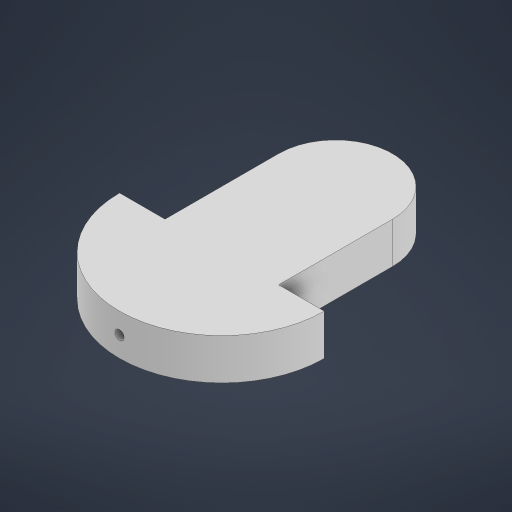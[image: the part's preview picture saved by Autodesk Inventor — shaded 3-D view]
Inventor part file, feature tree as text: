
AUTODESK INVENTOR PART (.ipt)
format: ipt  version: 2024 (Build 280153000, 153)  size: 178,176 bytes
history: native  units: mm
features: extrude x2, sketch x2, other x1, plane x1
ambient origin geometry x8: Origin, YZ Plane, XZ Plane, XY Plane, X Axis, Y Axis, Z Axis, Center Point
bodies: Body1 (feature_tree)
feature tree (6):
  other  "Sólido1"
  extrude  "Extrusión1"  Depth=90.0mm
  plane  "Plano de trabajo2"
  extrude  "Extrusión2"  Depth=4.0mm
  sketch  "Boceto1"  dims[d3=50.0mm d4=90.0mm]
  sketch  "Boceto2"  dims[d7=18.0mm d8=0.0mm d9=4.0mm d10=9.0mm d11=150.0mm d12=0.0mm]
